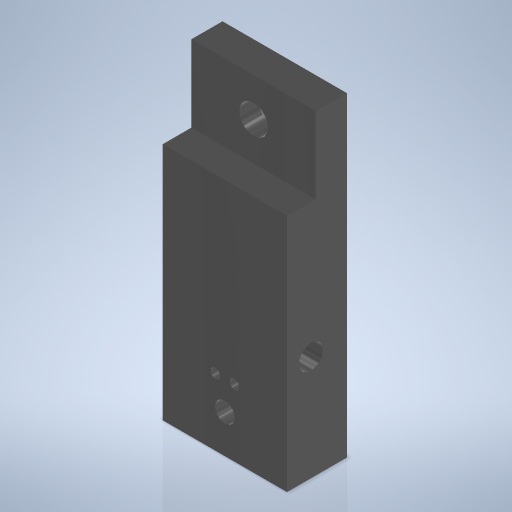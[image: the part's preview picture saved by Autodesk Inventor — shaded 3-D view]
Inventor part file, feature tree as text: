
AUTODESK INVENTOR PART (.ipt)
format: ipt  version: 2024 (Build 280153000, 153)  size: 302,592 bytes
history: native  units: mm
features: sketch x7, hole x6, extrude x2, mirror x1, chamfer x1
ambient origin geometry x8: Origin, YZ Plane, XZ Plane, XY Plane, X Axis, Y Axis, Z Axis, Center Point
bodies: Volumenkörper1 (feature_tree)
feature tree (17):
  extrude  "Extrusion1"  Depth=26.0mm
  extrude  "Extrusion2"  Depth=7.0mm
  hole  "Bohrung1"  [1 undecoded]
  hole  "Bohrung2"  [1 undecoded]
  hole  "Bohrung3"  [1 undecoded]
  sketch  "Skizze6"  dims[d16=4.134mm d17=10.0mm d18=12.0mm d19=2.0mm d20=90.0deg d21=8.0mm d22=0.0mm d23=8.0mm]
  hole  "Bohrung4"  [1 undecoded]
  hole  "Bohrung5"  [1 undecoded]
  mirror  "Spiegeln1"
  chamfer  "Fasen1"  Distance=14.0mm
  hole  "Bohrung6"  [1 undecoded]
  sketch  "Skizze1"  dims[d0=66.0mm d1=26.0mm]
  sketch  "Skizze2"  dims[d2=13.0mm d3=0.0mm d4=7.0mm]
  sketch  "Skizze3"  dims[d5=16.0mm d6=13.0mm d7=0.0mm]
  sketch  "Skizze4"  dims[d8=8.0mm]
  sketch  "Skizze5"  dims[d9=6.0mm d10=12.0mm d11=12.0mm d12=2.0mm d13=90.0deg d14=8.0mm d15=0.0mm]
  sketch  "Skizze7"  dims[d24=2.0mm d25=10.0mm d26=4.0mm d27=2.0mm d28=90.0deg d29=8.0mm d30=0.0mm d31=2.0mm d32=2.0mm d33=14.0mm d34=14.0mm d35=4.134mm d36=10.0mm d37=5.0mm d38=6.0mm d39=90.0deg d40=13.0mm d41=0.0mm d42=22.0mm d43=5.0mm d44=5.5mm d45=2.0mm d46=10.0mm d47=5.0mm d48=6.0mm d49=90.0deg d50=13.0mm d51=0.0mm d52=0.5mm d53=2.0mm d54=45.0deg d55=4.917mm d56=12.0mm d57=4.0mm d58=2.0mm d59=90.0deg d60=15.0mm d61=0.0mm d62=5.0mm d63=16.0mm d64=6.5mm]
note: 6 required parameter values undecoded (feature->parameter linkage not recoverable at this tier; creation-order binding heuristic only, values carry confidence <= 0.55)
